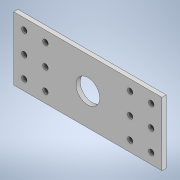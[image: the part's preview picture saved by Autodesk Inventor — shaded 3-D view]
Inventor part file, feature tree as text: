
AUTODESK INVENTOR PART (.ipt)
format: ipt  version: 2020 (Build 240168000, 168)  size: 129,536 bytes
history: native  units: in
note: dims shown in document units (in); Inventor stores cm internally (conversion verified against a paired STEP export)
features: extrude x1, sketch x1
ambient origin geometry x8: Origin, YZ Plane, XZ Plane, XY Plane, X Axis, Y Axis, Z Axis, Center Point
bodies: Body1 (feature_tree)
feature tree (2):
  extrude  "Extrusion2"  Depth=3.0in
  sketch  "Sketch1"  dims[d0=7.0in d1=3.0in d2=1.5in d3=3.5in d4=1.125in d5=0.256in d6=0.5in d7=0.5in d8=0.7874in d10=1.0in d11=1.1811in d13=1.0in d18=0.7874in d20=5.0in d21=0.3937in d23=1.0in d25=0.2in d26=0.0in]
